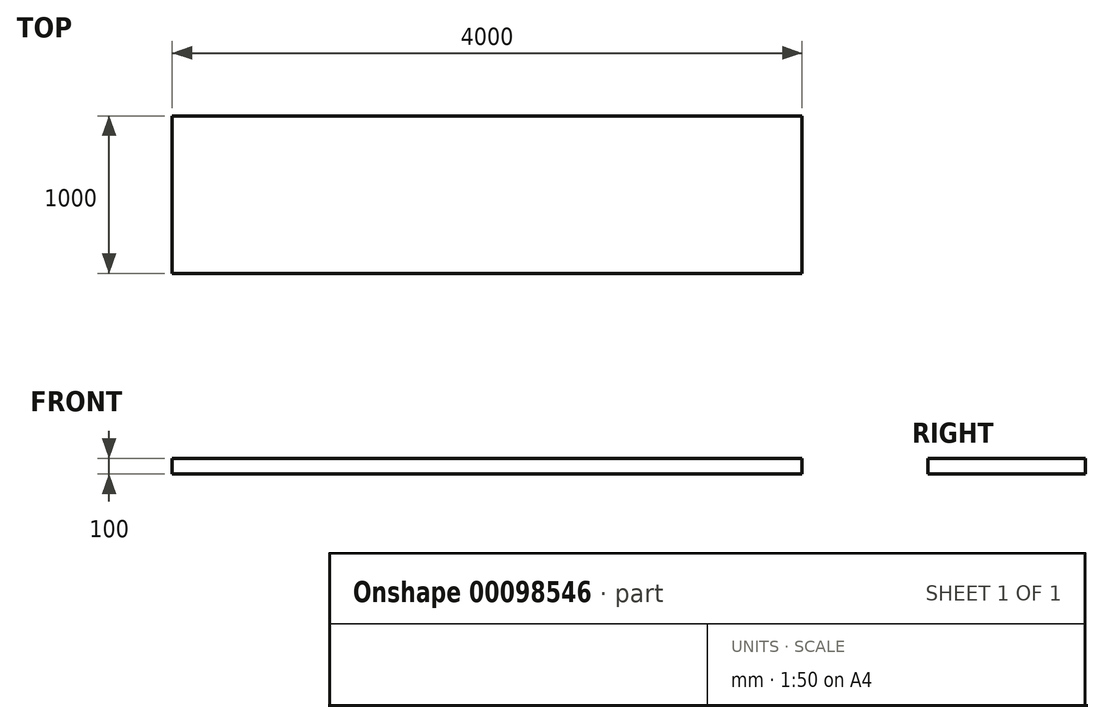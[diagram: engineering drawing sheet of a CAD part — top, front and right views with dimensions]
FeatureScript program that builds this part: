
annotation { "Feature Type Name" : "Feature", "Feature Type Description" : "" }
export const myFeature = defineFeature(function(context is Context, id is Id, definition is map)
    precondition{}
    {
        {
            var Q0;
            Q0=qCreatedBy(makeId("Top.planeOp"),FACE);
            var sketch = newSketch(context, id + "F0", { "sketchPlane" : qUnion([Q0])});
            skLineSegment(sketch, "E0.bottom", {"start": v(0, 0) * mm, "end": v(4000, 0) * mm});
            skLineSegment(sketch, "E0.top", {"start": v(0, 1000) * mm, "end": v(4000, 1000) * mm});
            skLineSegment(sketch, "E0.left", {"start": v(0, 0) * mm, "end": v(0, 1000) * mm});
            skLineSegment(sketch, "E0.right", {"start": v(4000, 0) * mm, "end": v(4000, 1000) * mm});
            skSolve(sketch);
        }
        {
            var Q0;
            Q0=makeQuery(id+"F0.imprint","IMPRINT",FACE,{"disambiguationData":[TD([[makeQuery(id+"F0.imprint","IMPRINT",EDGE,{"derivedFrom":sQuery(id+"F0.wireOp",EDGE,"E0.bottom")}),1.0]])]});
            extrude(context, id + "F1", {"entities" : qUnion([Q0]), "depth" : 100 * mm});
        }
    });
